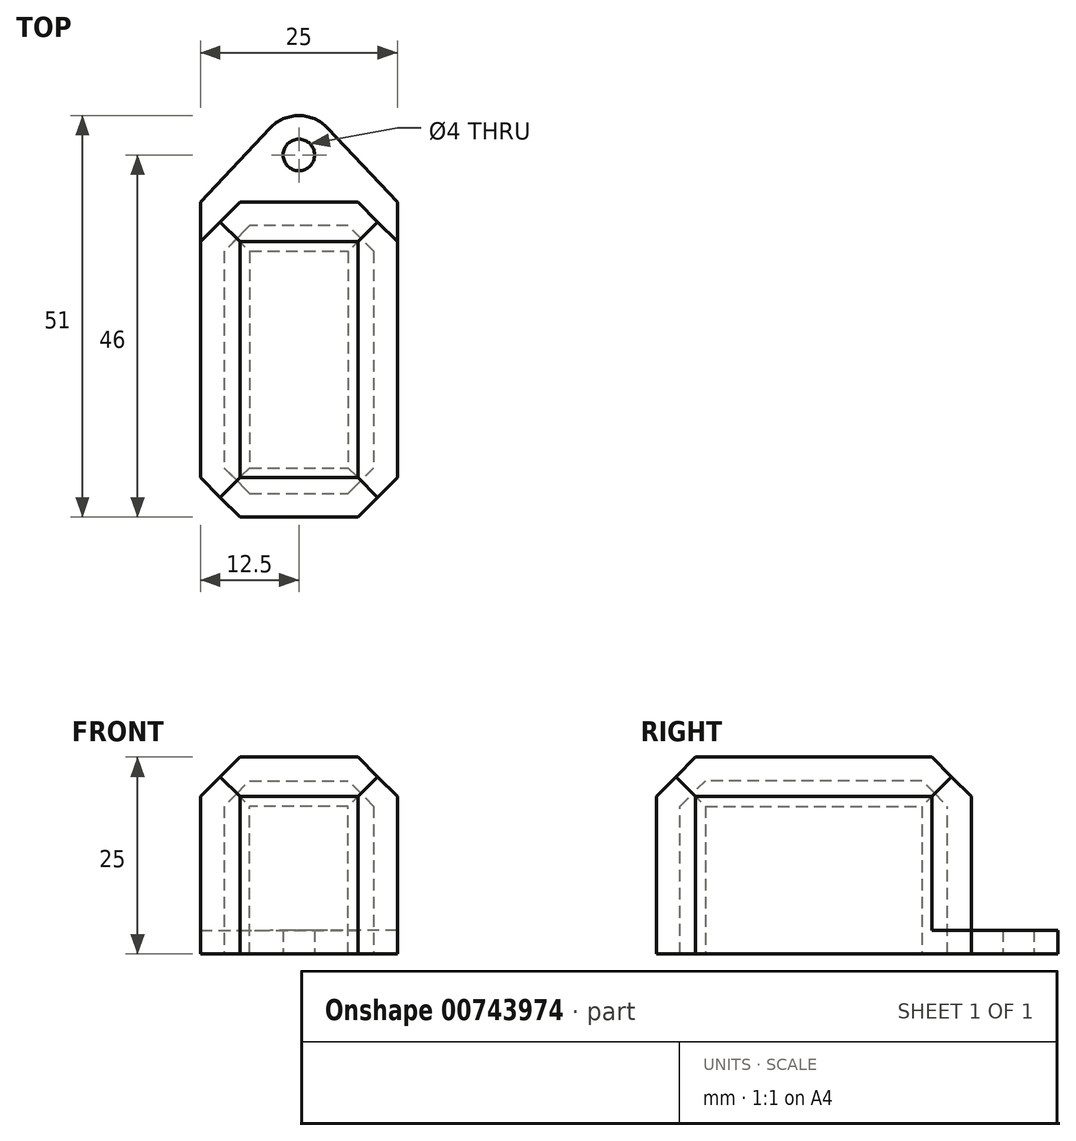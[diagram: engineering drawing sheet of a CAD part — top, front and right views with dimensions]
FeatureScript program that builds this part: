
annotation { "Feature Type Name" : "Feature", "Feature Type Description" : "" }
export const myFeature = defineFeature(function(context is Context, id is Id, definition is map)
    precondition{}
    {
        {
            var Q0;
            Q0=qCreatedBy(makeId("Top.planeOp"),FACE);
            var sketch = newSketch(context, id + "F0", { "sketchPlane" : qUnion([Q0])});
            skLineSegment(sketch, "E0.bottom", {"start": v(-12.5, 20) * mm, "end": v(12.5, 20) * mm});
            skLineSegment(sketch, "E0.top", {"start": v(-12.5, -20) * mm, "end": v(12.5, -20) * mm});
            skLineSegment(sketch, "E0.left", {"start": v(-12.5, 20) * mm, "end": v(-12.5, -20) * mm});
            skLineSegment(sketch, "E0.right", {"start": v(12.5, 20) * mm, "end": v(12.5, -20) * mm});
            skPoint(sketch, "E0.middle", {"position": v(0, 0) * mm});
            skCircle(sketch, "E1", {"center": v(0, 26) * mm, "radius": 5 * mm});
            skLineSegment(sketch, "E2", {"start": v(-12.5, 20) * mm, "end": v(-3.64, 29.42) * mm});
            skLineSegment(sketch, "E3", {"start": v(12.5, 20) * mm, "end": v(3.64, 29.42) * mm});
            skCircle(sketch, "E4", {"center": v(0, 26) * mm, "radius": 2 * mm});
            skSolve(sketch);
        }
        {
            var Q0;
            Q0=makeQuery(id+"F0.imprint","IMPRINT",FACE,{"disambiguationData":[TD([[makeQuery(id+"F0.imprint","IMPRINT",EDGE,{"derivedFrom":sQuery(id+"F0.wireOp",EDGE,"E0.bottom")}),-1.0]])]});
            extrude(context, id + "F1", {"entities" : qUnion([Q0]), "depth" : 25 * mm, "offsetDistance" : 25 * mm});
        }
        {
            var Q0;
            Q0=makeQuery(id+"F0.imprint","IMPRINT",FACE,{"disambiguationData":[TD([[makeQuery(id+"F0.imprint","IMPRINT",EDGE,{"derivedFrom":sQuery(id+"F0.wireOp",EDGE,"E0.bottom")}),1.0]])]});
            var Q1;
            Q1=makeQuery(id+"F0.imprint","IMPRINT",FACE,{"disambiguationData":[TD([[makeQuery(id+"F0.imprint","IMPRINT",EDGE,{"derivedFrom":sQuery(id+"F0.wireOp",EDGE,"E4")}),-1.0]])]});
            extrude(context, id + "F2", {"entities" : qUnion([Q0, Q1]), "operationType" : NewBodyOperationType.ADD, "depth" : 3 * mm, "offsetDistance" : 25 * mm});
        }
        {
            var Q0;
            Q0=makeQuery(id+"F1.opExtrude","CAP_EDGE",EDGE,{"disambiguationData":[OSD([sQuery(id+"F0.wireOp",EDGE,"E0.right")])],"isStart":false});
            var Q1;
            Q1=makeQuery(id+"F1.opExtrude","CAP_EDGE",EDGE,{"disambiguationData":[OSD([sQuery(id+"F0.wireOp",EDGE,"E0.top")])],"isStart":false});
            var Q2;
            Q2=makeQuery(id+"F1.opExtrude","CAP_EDGE",EDGE,{"disambiguationData":[OSD([sQuery(id+"F0.wireOp",EDGE,"E0.left")])],"isStart":false});
            var Q3;
            Q3=makeQuery(id+"F1.opExtrude","CAP_EDGE",EDGE,{"disambiguationData":[OSD([sQuery(id+"F0.wireOp",EDGE,"E0.bottom")])],"isStart":false});
            chamfer(context, id + "F3", {"entities" : qUnion([Q0, Q1, Q2, Q3]), "width" : 5 * mm, "tangentPropagation" : true});
        }
        {
            var Q0;
            Q0=makeQuery(id+"F1.opExtrude","SWEPT_EDGE",EDGE,{"disambiguationData":[OSD([sQuery(id+"F0.wireOp",EDGE,"E0.top"),sQuery(id+"F0.wireOp",EDGE,"E0.left")])]});
            var Q1;
            Q1=makeQuery(id+"F1.opExtrude","SWEPT_EDGE",EDGE,{"disambiguationData":[OSD([sQuery(id+"F0.wireOp",EDGE,"E0.top"),sQuery(id+"F0.wireOp",EDGE,"E0.right")])]});
            var Q2;
            Q2=makeQuery(id+"F2.boolean.opBoolean","SPLIT",EDGE,{"derivedFrom":makeQuery(id+"F1.opExtrude","SWEPT_EDGE",EDGE,{"disambiguationData":[OSD([sQuery(id+"F0.wireOp",EDGE,"E0.bottom"),sQuery(id+"F0.wireOp",EDGE,"E0.right"),sQuery(id+"F0.wireOp",EDGE,"E3")])]})});
            var Q3;
            Q3=makeQuery(id+"F2.boolean.opBoolean","SPLIT",EDGE,{"derivedFrom":makeQuery(id+"F1.opExtrude","SWEPT_EDGE",EDGE,{"disambiguationData":[OSD([sQuery(id+"F0.wireOp",EDGE,"E0.bottom"),sQuery(id+"F0.wireOp",EDGE,"E0.left"),sQuery(id+"F0.wireOp",EDGE,"E2")])]})});
            chamfer(context, id + "F4", {"entities" : qUnion([Q0, Q1, Q2, Q3]), "width" : 5 * mm, "tangentPropagation" : true});
        }
        {
            var Q0;
            {var subQ0=sQuery(id+"F0.wireOp",EDGE,"E0.bottom");Q0=makeQuery(id+"F2.boolean.opBoolean","MERGE",FACE,{"derivedFrom":[makeQuery(id+"F1.opExtrude","CAP_FACE",FACE,{"disambiguationData":[OSD([subQ0,sQuery(id+"F0.wireOp",EDGE,"E0.top"),sQuery(id+"F0.wireOp",EDGE,"E0.left"),sQuery(id+"F0.wireOp",EDGE,"E0.right")])],"isStart":true}),makeQuery(id+"F2.opExtrude","CAP_FACE",FACE,{"disambiguationData":[OSD([subQ0,sQuery(id+"F0.wireOp",EDGE,"E1"),sQuery(id+"F0.wireOp",EDGE,"E2"),sQuery(id+"F0.wireOp",EDGE,"E3"),sQuery(id+"F0.wireOp",EDGE,"E4")])],"isStart":true})]});}
            shell(context, id + "F5", {"entities" : qUnion([Q0]), "thickness" : 3 * mm});
        }
    });
